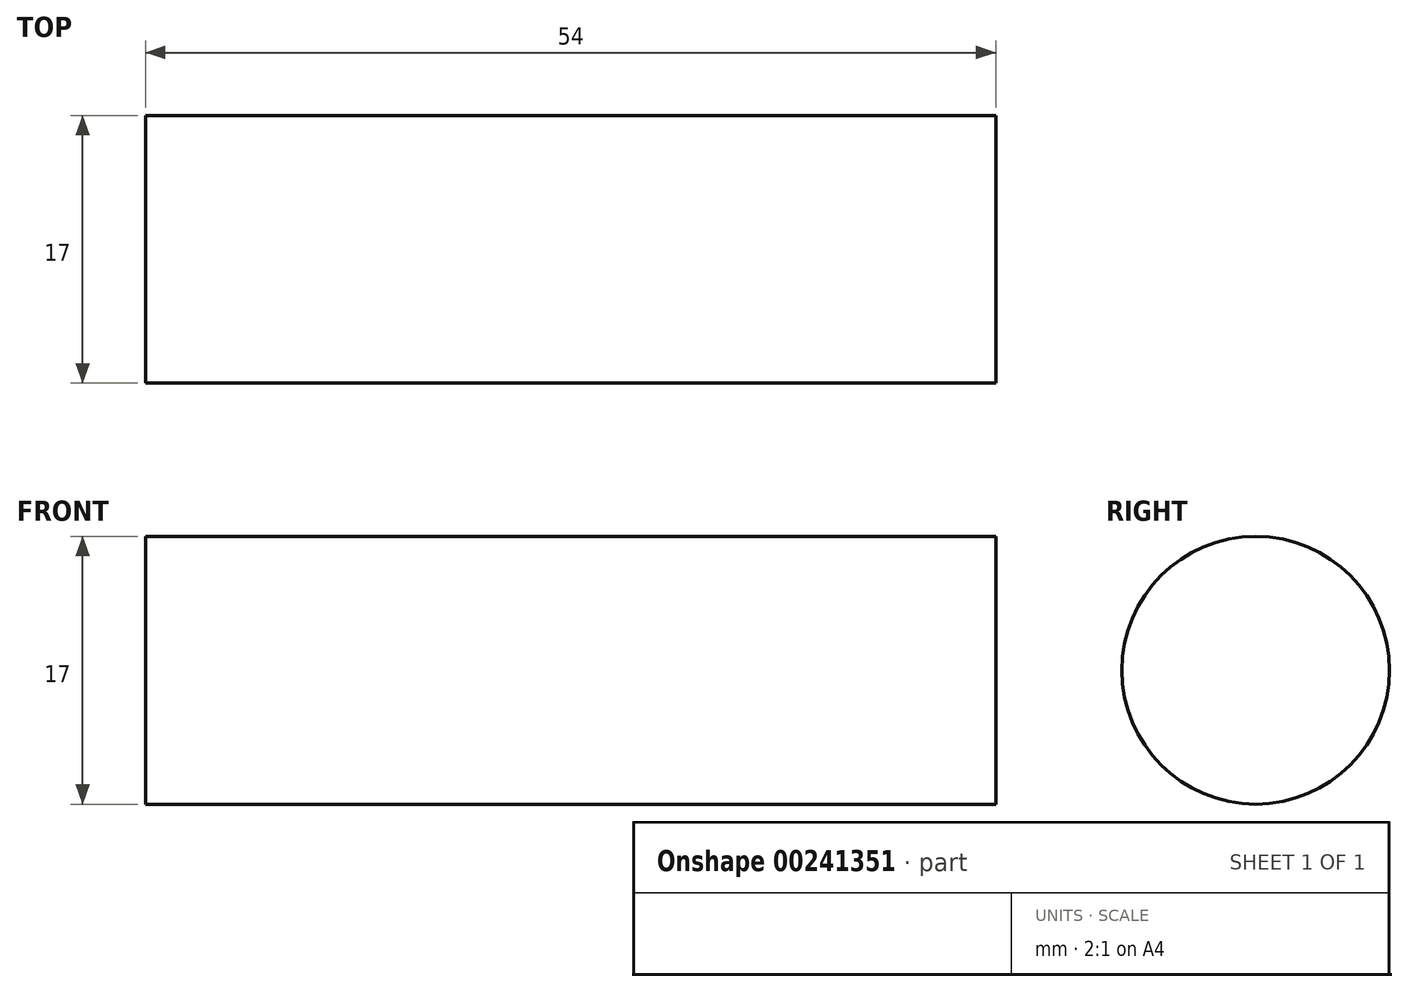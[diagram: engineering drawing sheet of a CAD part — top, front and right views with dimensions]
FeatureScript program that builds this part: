
annotation { "Feature Type Name" : "Feature", "Feature Type Description" : "" }
export const myFeature = defineFeature(function(context is Context, id is Id, definition is map)
    precondition{}
    {
        {
            var Q0;
            Q0=qCreatedBy(makeId("Right.planeOp"),FACE);
            var sketch = newSketch(context, id + "F0", { "sketchPlane" : qUnion([Q0])});
            skCircle(sketch, "E0", {"center": v(0, 0) * mm, "radius": 8.5 * mm});
            skSolve(sketch);
        }
        {
            var Q0;
            Q0 = qSketchRegion(id + "F0", true);
            extrude(context, id + "F1", {"entities" : qUnion([Q0]), "depth" : 54 * mm});
        }
    });
